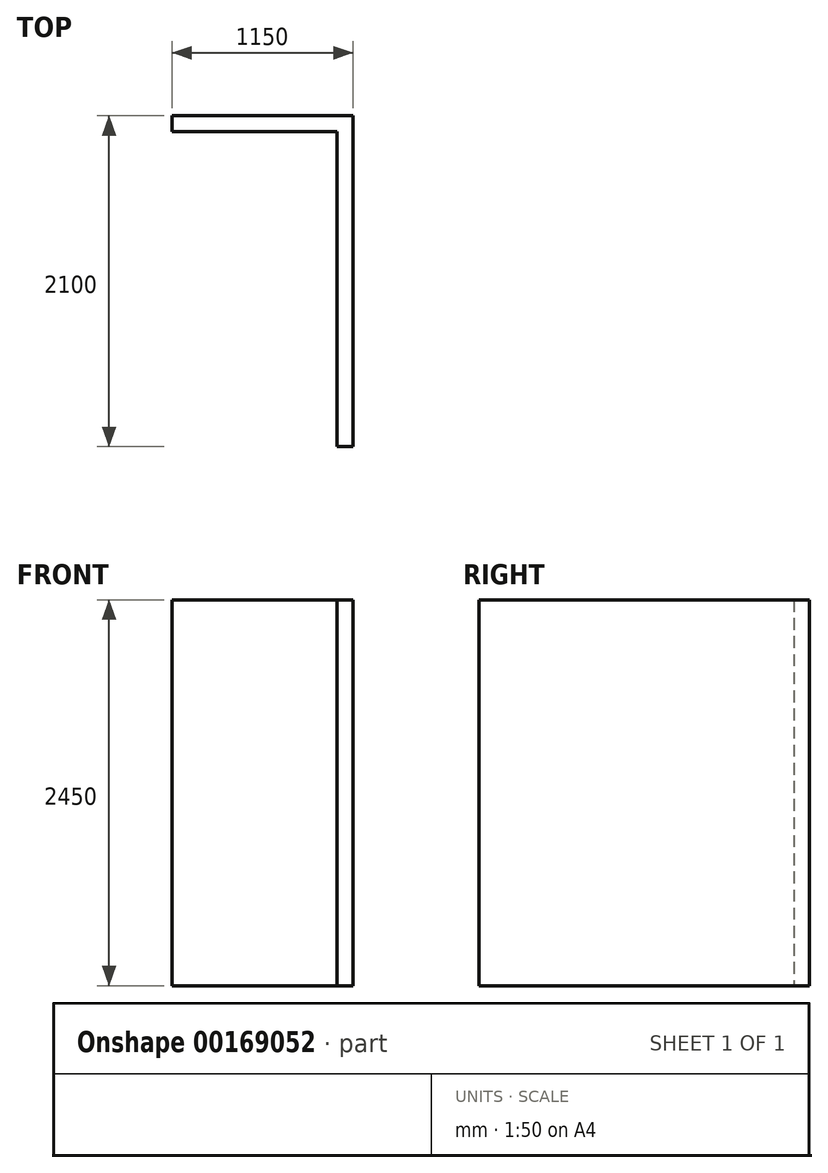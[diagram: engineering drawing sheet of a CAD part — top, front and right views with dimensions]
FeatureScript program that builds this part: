
annotation { "Feature Type Name" : "Feature", "Feature Type Description" : "" }
export const myFeature = defineFeature(function(context is Context, id is Id, definition is map)
    precondition{}
    {
        {
            var Q0;
            Q0=qCreatedBy(makeId("Top.planeOp"),FACE);
            var sketch = newSketch(context, id + "F0", { "sketchPlane" : qUnion([Q0])});
            skLineSegment(sketch, "E0", {"start": v(0, 0) * mm, "end": v(-1050, 0) * mm});
            skLineSegment(sketch, "E1", {"start": v(0, 0) * mm, "end": v(0, -2000) * mm});
            skLineSegment(sketch, "E2.0", {"start": v(100, 100) * mm, "end": v(-1050, 100) * mm});
            skLineSegment(sketch, "E2.1", {"start": v(100, 100) * mm, "end": v(100, -2000) * mm});
            skLineSegment(sketch, "E3", {"start": v(-1050, 100) * mm, "end": v(-1050, 0) * mm});
            skLineSegment(sketch, "E4", {"start": v(0, -2000) * mm, "end": v(100, -2000) * mm});
            skSolve(sketch);
        }
        {
            var Q0;
            Q0=makeQuery(id+"F0.imprint","IMPRINT",FACE,{"disambiguationData":[TD([[makeQuery(id+"F0.imprint","IMPRINT",EDGE,{"derivedFrom":sQuery(id+"F0.wireOp",EDGE,"E0")}),-1.0]])]});
            extrude(context, id + "F1", {"entities" : qUnion([Q0]), "depth" : 2450 * mm});
        }
    });
